# Revit family: Basin-Wall-Stylus Venecia 500 Vanity1
name_source: partatom
category: Plumbing Fixtures
revit_build: Autodesk Revit Architecture 2012 (Build: 20110916_2132(x64)
units: mm (PartAtom-declared; Revit-internal decimal feet)

## types (1)
- 3 Tap Holes with Shroud
    1 Taphole = No
    3 Tapholes = Yes
    Assembly Code = C1030210
    CW Connection = No
    Cost = 167.4 $
    Default Elevation = 870 mm  [stored 2.85433 ft]
    Description = Venecia 500 Wall Basin
    HW Connection = No
    Keynote = HB
    Manufacturer = Stylus
    Material_ANZRS = Porcelain-White-Caroma
    Model = W40303C
    Pedestal = No
    PlumbingMaterial_ANZRS = PVC-White-Caroma
    Shroud = Yes
    Spout Penetration = 0 mm  [stored 0 ft]
    Tap Penetrations = 0 mm  [stored 0 ft]
    Type Comments = Vitreous China Wall Basin
    URL = http://www.stylus.com.au
    Vent Connection = No
    Waste = Metal-Chrome-Caroma
    Waste Connection = Yes

note: [stored X ft] marks values corroborated as IEEE doubles in the binary element streams (Revit-internal decimal feet)

## geometry (parser evidence)
native form markers: Blend x6, Sweep x9
no freeform markers — native parametric forms only
